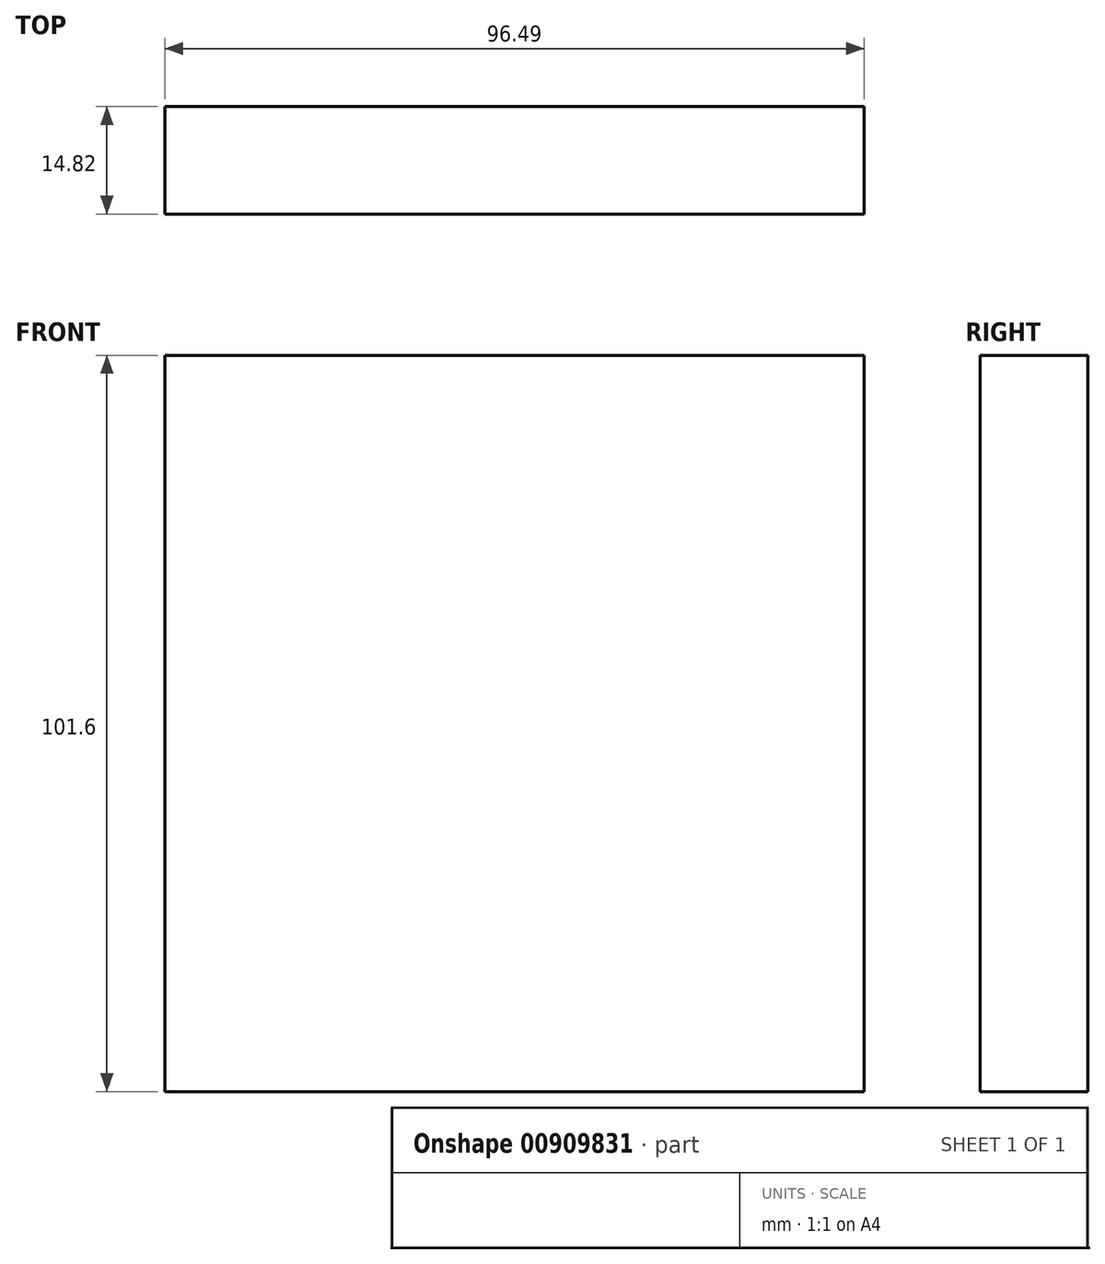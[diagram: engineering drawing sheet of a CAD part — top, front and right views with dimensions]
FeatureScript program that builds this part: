
annotation { "Feature Type Name" : "Feature", "Feature Type Description" : "" }
export const myFeature = defineFeature(function(context is Context, id is Id, definition is map)
    precondition{}
    {
        {
            var Q0;
            Q0=qCreatedBy(makeId("Top.planeOp"),FACE);
            var sketch = newSketch(context, id + "F0", { "sketchPlane" : qUnion([Q0])});
            skLineSegment(sketch, "E0.bottom", {"start": v(-127.06, -29.4) * mm, "end": v(-30.57, -29.4) * mm});
            skLineSegment(sketch, "E0.top", {"start": v(-127.06, -44.21) * mm, "end": v(-30.57, -44.21) * mm});
            skLineSegment(sketch, "E0.left", {"start": v(-127.06, -29.4) * mm, "end": v(-127.06, -44.21) * mm});
            skLineSegment(sketch, "E0.right", {"start": v(-30.57, -29.4) * mm, "end": v(-30.57, -44.21) * mm});
            skSolve(sketch);
        }
        {
            var Q0;
            Q0=makeQuery(id+"F0.imprint","IMPRINT",FACE,{"disambiguationData":[TD([[makeQuery(id+"F0.imprint","IMPRINT",EDGE,{"derivedFrom":sQuery(id+"F0.wireOp",EDGE,"E0.bottom")}),-1.0]])]});
            extrude(context, id + "F1", {"entities" : qUnion([Q0]), "depth" : 101.6 * mm, "offsetDistance" : 25.4 * mm});
        }
    });
